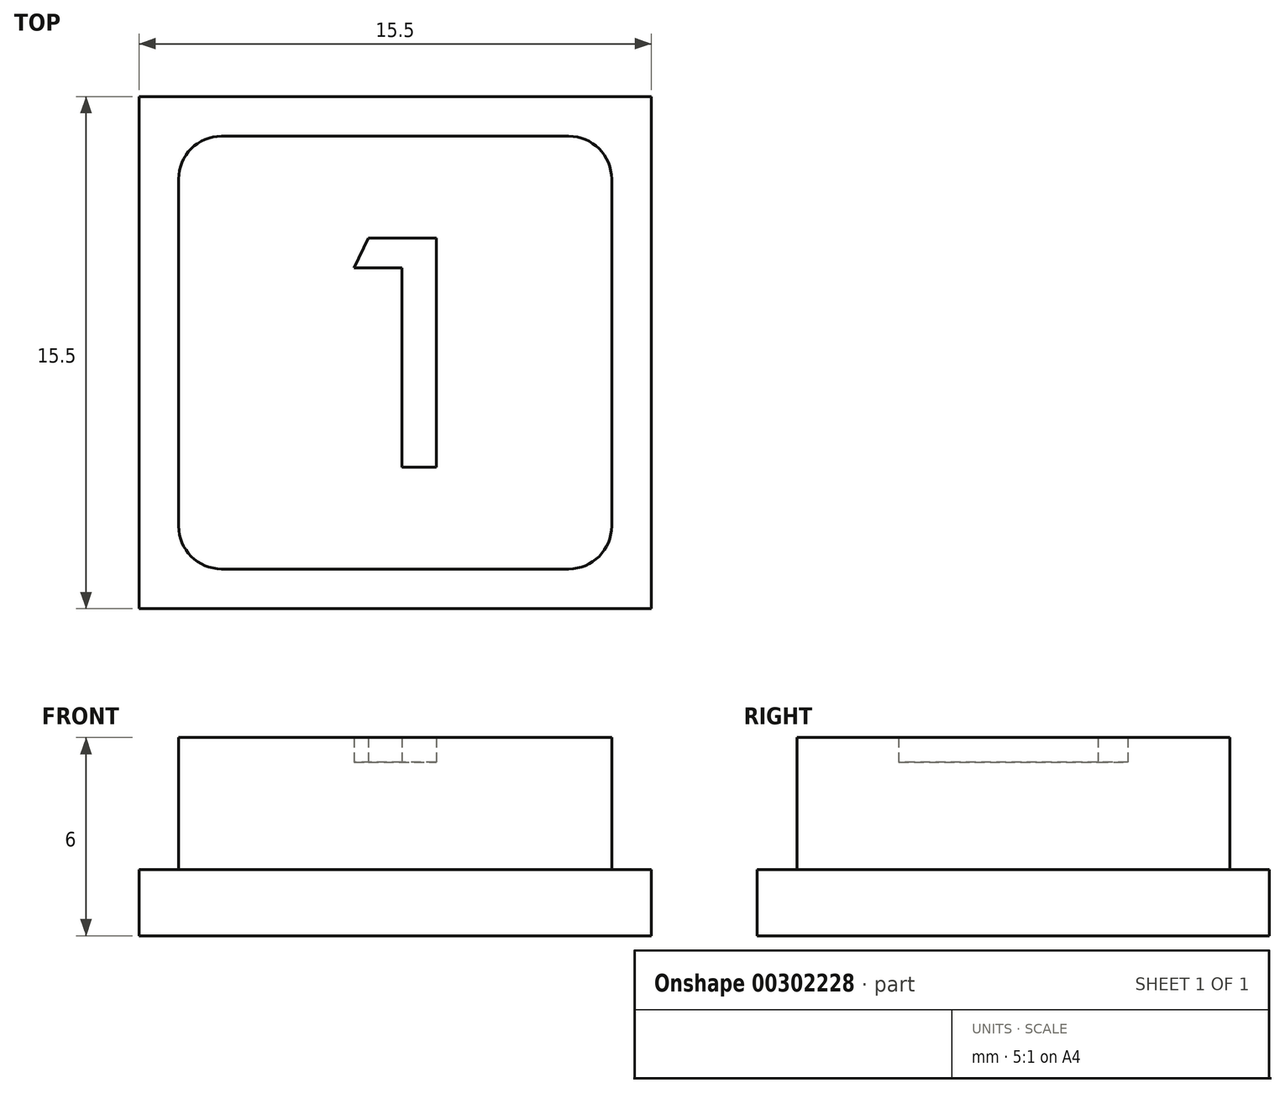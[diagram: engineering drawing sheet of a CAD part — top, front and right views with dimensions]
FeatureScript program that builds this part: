
annotation { "Feature Type Name" : "Feature", "Feature Type Description" : "" }
export const myFeature = defineFeature(function(context is Context, id is Id, definition is map)
    precondition{}
    {
        {
            var Q0;
            Q0=qCreatedBy(makeId("Top.planeOp"),FACE);
            var sketch = newSketch(context, id + "F0", { "sketchPlane" : qUnion([Q0])});
            skLineSegment(sketch, "E0", {"start": v(-7.75, 7.75) * mm, "end": v(-7.75, -7.75) * mm});
            skLineSegment(sketch, "E1", {"start": v(-7.75, -7.75) * mm, "end": v(7.75, -7.75) * mm});
            skLineSegment(sketch, "E2", {"start": v(7.75, -7.75) * mm, "end": v(7.75, 7.75) * mm});
            skLineSegment(sketch, "E3", {"start": v(7.75, 7.75) * mm, "end": v(-7.75, 7.75) * mm});
            skLineSegment(sketch, "E4", {"start": v(0.2, -3.47) * mm, "end": v(0.2, 2.57) * mm});
            skLineSegment(sketch, "E5", {"start": v(0.2, 2.57) * mm, "end": v(-1.24, 2.57) * mm});
            skLineSegment(sketch, "E6", {"start": v(-1.24, 2.57) * mm, "end": v(-0.8, 3.47) * mm});
            skLineSegment(sketch, "E7", {"start": v(-0.8, 3.47) * mm, "end": v(1.24, 3.47) * mm});
            skLineSegment(sketch, "E8", {"start": v(1.24, 3.47) * mm, "end": v(1.24, -3.47) * mm});
            skLineSegment(sketch, "E9", {"start": v(1.24, -3.47) * mm, "end": v(0.2, -3.47) * mm});
            skLineSegment(sketch, "E10", {"start": v(-6.55, 5.25) * mm, "end": v(-6.55, -5.25) * mm});
            skArc(sketch, "E11", {"start": v(-6.55, -5.25) * mm, "mid": v(-6.17, -6.17) * mm, "end": v(-5.25, -6.55) * mm});
            skLineSegment(sketch, "E12", {"start": v(-5.25, -6.55) * mm, "end": v(5.25, -6.55) * mm});
            skArc(sketch, "E13", {"start": v(5.25, -6.55) * mm, "mid": v(6.17, -6.17) * mm, "end": v(6.55, -5.25) * mm});
            skLineSegment(sketch, "E14", {"start": v(6.55, -5.25) * mm, "end": v(6.55, 5.25) * mm});
            skArc(sketch, "E15", {"start": v(6.55, 5.25) * mm, "mid": v(6.17, 6.17) * mm, "end": v(5.25, 6.55) * mm});
            skLineSegment(sketch, "E16", {"start": v(5.25, 6.55) * mm, "end": v(-5.25, 6.55) * mm});
            skArc(sketch, "E17", {"start": v(-5.25, 6.55) * mm, "mid": v(-6.17, 6.17) * mm, "end": v(-6.55, 5.25) * mm});
            skSolve(sketch);
        }
        {
            var Q0;
            Q0 = qSketchRegion(id + "F0", true);
            extrude(context, id + "F1", {"entities" : qUnion([Q0]), "depth" : 2 * mm});
        }
        {
            var Q0;
            Q0=makeQuery(id+"F0.imprint","IMPRINT",FACE,{"disambiguationData":[TD([[makeQuery(id+"F0.imprint","IMPRINT",EDGE,{"derivedFrom":sQuery(id+"F0.wireOp",EDGE,"E4")}),1.0]])]});
            extrude(context, id + "F2", {"entities" : qUnion([Q0]), "operationType" : NewBodyOperationType.ADD, "depth" : 6 * mm});
        }
        {
            var Q0;
            Q0=makeQuery(id+"F0.imprint","IMPRINT",FACE,{"disambiguationData":[TD([[makeQuery(id+"F0.imprint","IMPRINT",EDGE,{"derivedFrom":sQuery(id+"F0.wireOp",EDGE,"E4")}),-1.0]])]});
            extrude(context, id + "F3", {"entities" : qUnion([Q0]), "operationType" : NewBodyOperationType.ADD, "depth" : 5.25 * mm});
        }
    });
